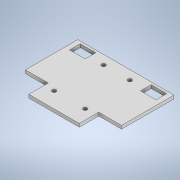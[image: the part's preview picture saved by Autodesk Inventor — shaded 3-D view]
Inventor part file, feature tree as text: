
AUTODESK INVENTOR PART (.ipt)
format: ipt  version: 2021 (Build 250183000, 183)  size: 137,216 bytes
history: native  units: mm
features: other x1, extrude x1, sketch x1
ambient origin geometry x8: Origin, YZ Plane, XZ Plane, XY Plane, X Axis, Y Axis, Z Axis, Center Point
bodies: Body1 (feature_tree)
feature tree (3):
  other  "Sólido1"
  extrude  "Extrusión1"  Depth=99.0mm
  sketch  "Boceto1"  dims[d0=54.0mm d1=99.0mm d2=20.0mm d3=52.0mm d4=23.5mm d5=23.5mm d6=4.0mm d7=16.0mm d8=10.0mm d9=2.5mm d10=5.0mm d11=11.0mm d12=16.0mm d13=4.0mm d15=9.5mm d16=3.4mm d17=0.0mm d18=34.0mm d19=15.0mm]
